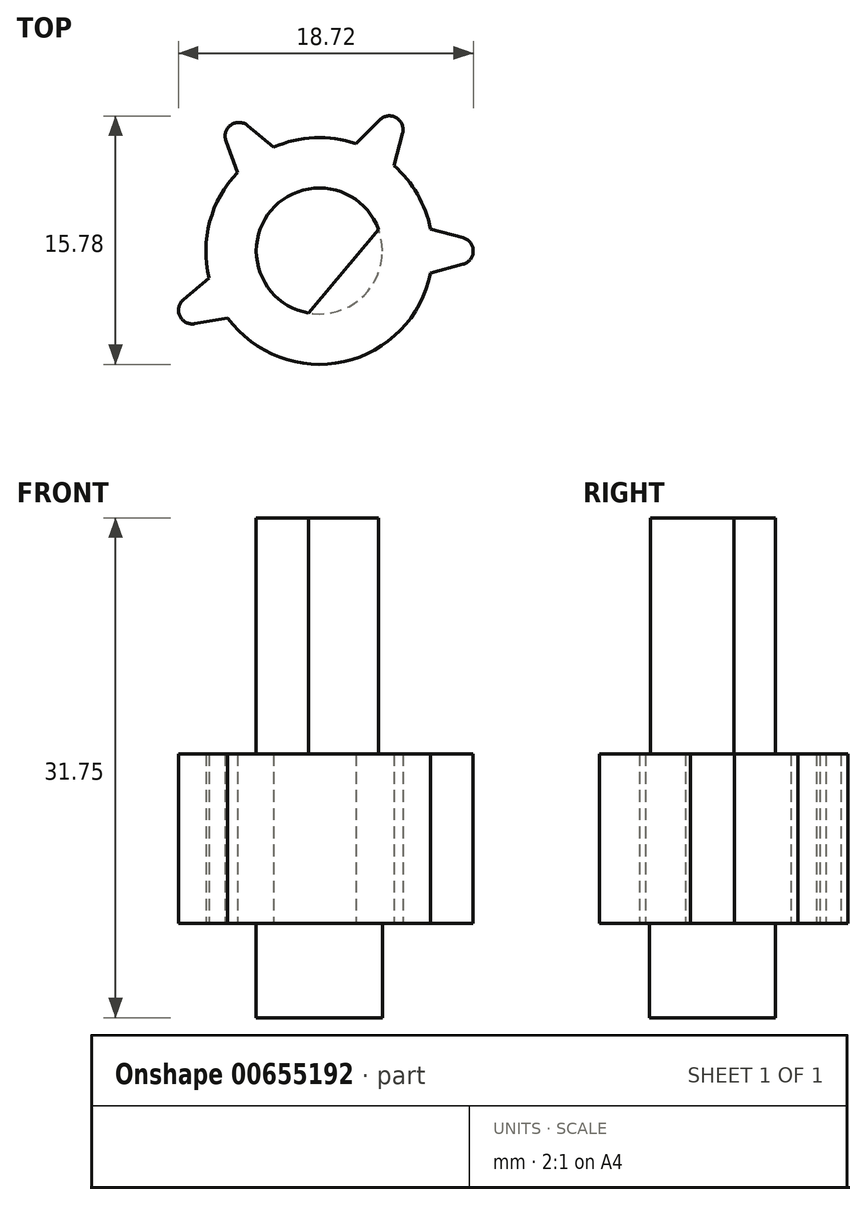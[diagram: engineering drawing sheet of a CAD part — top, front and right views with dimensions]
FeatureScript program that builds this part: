
annotation { "Feature Type Name" : "Feature", "Feature Type Description" : "" }
export const myFeature = defineFeature(function(context is Context, id is Id, definition is map)
    precondition{}
    {
        {
            var Q0;
            Q0=qCreatedBy(makeId("Top.planeOp"),FACE);
            var sketch = newSketch(context, id + "F0", { "sketchPlane" : qUnion([Q0])});
            skCircle(sketch, "E0", {"center": v(0, 0) * mm, "radius": 7.2 * mm});
            skLineSegment(sketch, "E1", {"start": v(0, 0) * mm, "end": v(-8.07, -3.76) * mm});
            skLineSegment(sketch, "E2", {"start": v(0, 0) * mm, "end": v(8.9, 0) * mm});
            skLineSegment(sketch, "E3", {"start": v(0, 0) * mm, "end": v(4.45, 7.7) * mm});
            skLineSegment(sketch, "E4", {"start": v(0, 0) * mm, "end": v(-5.1, 7.3) * mm});
            skCircle(sketch, "E5", {"center": v(-5.1, 7.3) * mm, "radius": 0.88 * mm});
            skCircle(sketch, "E6", {"center": v(4.45, 7.7) * mm, "radius": 0.88 * mm});
            skCircle(sketch, "E7", {"center": v(8.9, 0) * mm, "radius": 0.88 * mm});
            skLineSegment(sketch, "E8", {"start": v(4.45, 7.7) * mm, "end": v(5.2, 7.27) * mm, "construction": true});
            skLineSegment(sketch, "E9", {"start": v(4.45, 7.7) * mm, "end": v(3.7, 8.15) * mm, "construction": true});
            skLineSegment(sketch, "E10", {"start": v(-5.1, 7.3) * mm, "end": v(-4.39, 7.8) * mm, "construction": true});
            skLineSegment(sketch, "E11", {"start": v(-5.1, 7.3) * mm, "end": v(-5.82, 6.79) * mm, "construction": true});
            skLineSegment(sketch, "E12", {"start": v(-5.1, 7.3) * mm, "end": v(-4.54, 7.96) * mm, "construction": true});
            skLineSegment(sketch, "E13", {"start": v(-5.1, 7.3) * mm, "end": v(-5.93, 7) * mm, "construction": true});
            skLineSegment(sketch, "E14", {"start": v(8.9, 0) * mm, "end": v(8.9, -0.88) * mm, "construction": true});
            skLineSegment(sketch, "E15", {"start": v(8.9, 0) * mm, "end": v(8.9, 0.88) * mm, "construction": true});
            skLineSegment(sketch, "E16", {"start": v(8.9, 0) * mm, "end": v(9.13, 0.85) * mm});
            skLineSegment(sketch, "E17", {"start": v(8.9, 0) * mm, "end": v(9.13, -0.85) * mm});
            skLineSegment(sketch, "E18", {"start": v(4.45, 7.7) * mm, "end": v(3.83, 8.33) * mm});
            skLineSegment(sketch, "E19", {"start": v(4.45, 7.7) * mm, "end": v(5.3, 7.48) * mm});
            skLineSegment(sketch, "E20", {"start": v(-5.93, 7) * mm, "end": v(-5.2, 4.98) * mm});
            skLineSegment(sketch, "E21", {"start": v(-4.54, 7.96) * mm, "end": v(-2.9, 6.59) * mm});
            skLineSegment(sketch, "E22", {"start": v(3.83, 8.33) * mm, "end": v(2.32, 6.82) * mm});
            skLineSegment(sketch, "E23", {"start": v(5.3, 7.48) * mm, "end": v(4.74, 5.42) * mm});
            skLineSegment(sketch, "E24", {"start": v(9.13, 0.85) * mm, "end": v(7.06, 1.4) * mm});
            skLineSegment(sketch, "E25", {"start": v(9.13, -0.85) * mm, "end": v(7.06, -1.4) * mm});
            skCircle(sketch, "E26", {"center": v(-8.07, -3.76) * mm, "radius": 0.88 * mm});
            skLineSegment(sketch, "E27", {"start": v(-8.07, -3.76) * mm, "end": v(-8.44, -2.97) * mm, "construction": true});
            skLineSegment(sketch, "E28", {"start": v(-8.07, -3.76) * mm, "end": v(-7.7, -4.55) * mm, "construction": true});
            skLineSegment(sketch, "E29", {"start": v(-8.07, -3.76) * mm, "end": v(-7.91, -4.62) * mm, "construction": true});
            skLineSegment(sketch, "E30", {"start": v(-8.07, -3.76) * mm, "end": v(-8.63, -3.1) * mm, "construction": true});
            skLineSegment(sketch, "E31", {"start": v(-8.63, -3.1) * mm, "end": v(-7, -1.72) * mm});
            skLineSegment(sketch, "E32", {"start": v(-7.91, -4.62) * mm, "end": v(-5.81, -4.25) * mm});
            skSolve(sketch);
        }
        {
            var Q0;
            Q0=qSketchRegion(id+"F0",true);
            extrude(context, id + "F1", {"entities" : qUnion([Q0]), "depth" : 10.75 * mm, "offsetDistance" : 25 * mm});
        }
        {
            var Q0;
            Q0=makeQuery(id+"F1.opExtrude","CAP_FACE",FACE,{"disambiguationData":[OSD([sQuery(id+"F0.wireOp",EDGE,"E0"),sQuery(id+"F0.wireOp",EDGE,"E5"),sQuery(id+"F0.wireOp",EDGE,"E6"),sQuery(id+"F0.wireOp",EDGE,"E7"),sQuery(id+"F0.wireOp",EDGE,"E20"),sQuery(id+"F0.wireOp",EDGE,"E21"),sQuery(id+"F0.wireOp",EDGE,"E22"),sQuery(id+"F0.wireOp",EDGE,"E23"),sQuery(id+"F0.wireOp",EDGE,"E24"),sQuery(id+"F0.wireOp",EDGE,"E25"),sQuery(id+"F0.wireOp",EDGE,"E26"),sQuery(id+"F0.wireOp",EDGE,"E31"),sQuery(id+"F0.wireOp",EDGE,"E32")])],"isStart":false});
            var sketch = newSketch(context, id + "F2", { "sketchPlane" : qUnion([Q0])});
            skCircle(sketch, "E33", {"center": v(0, 0) * mm, "radius": 4 * mm});
            skSolve(sketch);
        }
        {
            var Q0;
            Q0=qSketchRegion(id+"F2",true);
            extrude(context, id + "F3", {"entities" : qUnion([Q0]), "operationType" : NewBodyOperationType.ADD, "oppositeDirection" : true, "depth" : (6 + 10.75) * mm, "offsetDistance" : 25 * mm});
        }
        {
            var Q0;
            Q0=makeQuery(id+"F1.opExtrude","CAP_FACE",FACE,{"disambiguationData":[OSD([sQuery(id+"F0.wireOp",EDGE,"E0"),sQuery(id+"F0.wireOp",EDGE,"E5"),sQuery(id+"F0.wireOp",EDGE,"E6"),sQuery(id+"F0.wireOp",EDGE,"E7"),sQuery(id+"F0.wireOp",EDGE,"E20"),sQuery(id+"F0.wireOp",EDGE,"E21"),sQuery(id+"F0.wireOp",EDGE,"E22"),sQuery(id+"F0.wireOp",EDGE,"E23"),sQuery(id+"F0.wireOp",EDGE,"E24"),sQuery(id+"F0.wireOp",EDGE,"E25"),sQuery(id+"F0.wireOp",EDGE,"E26"),sQuery(id+"F0.wireOp",EDGE,"E31"),sQuery(id+"F0.wireOp",EDGE,"E32")])],"isStart":true});
            var sketch = newSketch(context, id + "F4", { "sketchPlane" : qUnion([Q0])});
            skArc(sketch, "E34", {"start": v(-0.7, 3.94) * mm, "mid": v(-3.06, -2.57) * mm, "end": v(3.76, -1.37) * mm});
            skLineSegment(sketch, "E35", {"start": v(0, 0) * mm, "end": v(2.61, 0) * mm, "construction": true});
            skLineSegment(sketch, "E36", {"start": v(2.61, 0) * mm, "end": v(-0.95, 4.25) * mm, "construction": true});
            skLineSegment(sketch, "E37", {"start": v(0, 0) * mm, "end": v(1.53, 1.29) * mm});
            skLineSegment(sketch, "E38", {"start": v(-0.7, 3.94) * mm, "end": v(3.76, -1.37) * mm});
            skSolve(sketch);
        }
        {
            var Q0;
            Q0=qSketchRegion(id+"F4",true);
            extrude(context, id + "F5", {"entities" : qUnion([Q0]), "operationType" : NewBodyOperationType.ADD, "oppositeDirection" : true, "depth" : (15 + 10.75) * mm, "offsetDistance" : 25 * mm});
        }
    });
